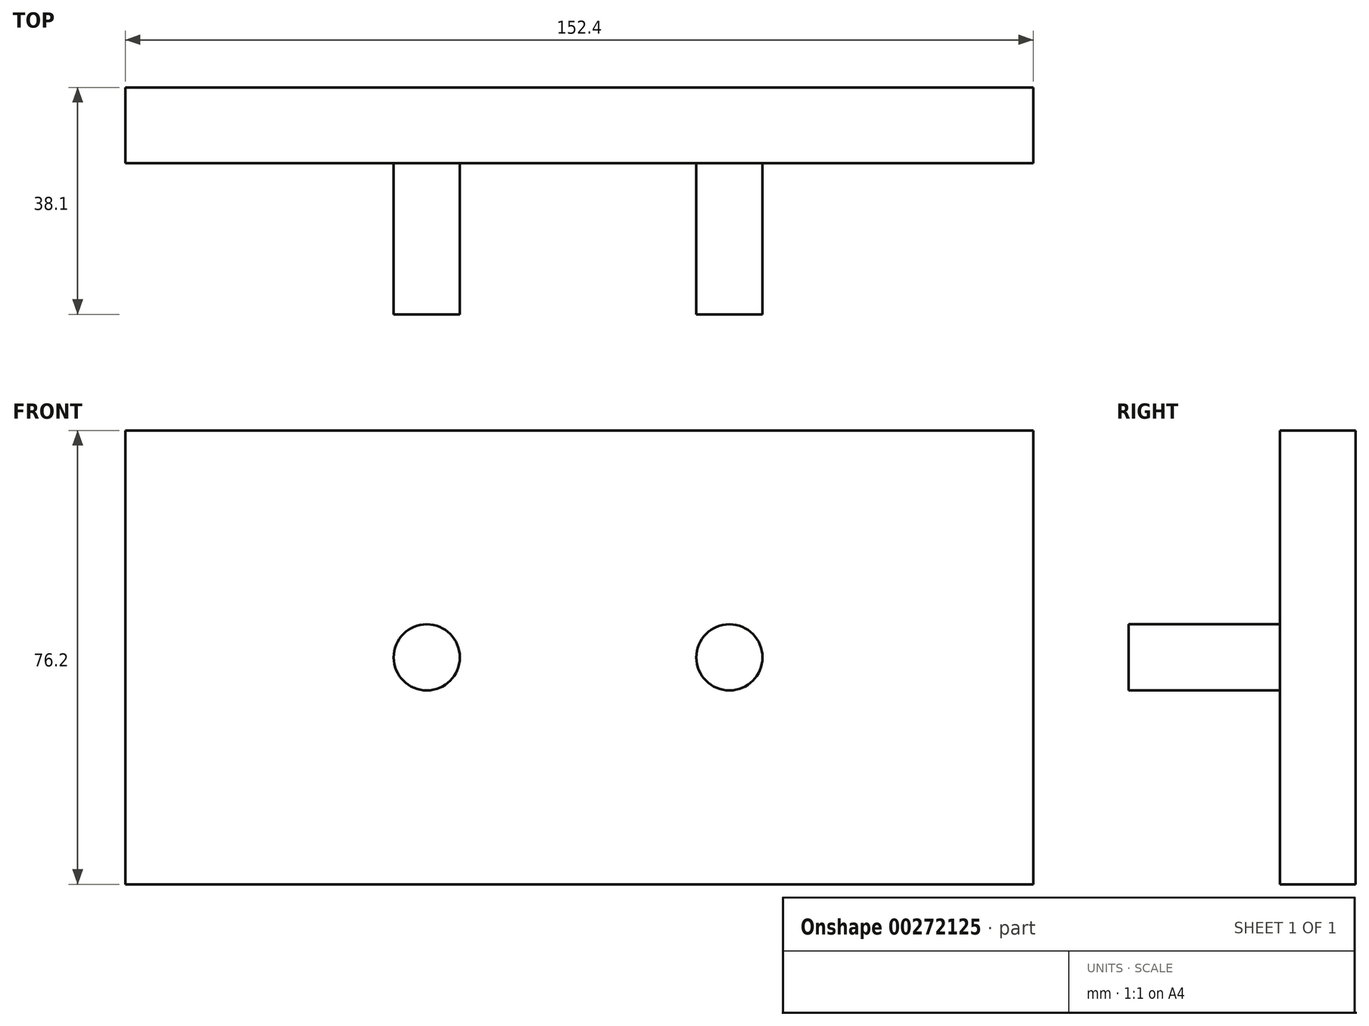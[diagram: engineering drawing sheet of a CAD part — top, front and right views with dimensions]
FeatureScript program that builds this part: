
annotation { "Feature Type Name" : "Feature", "Feature Type Description" : "" }
export const myFeature = defineFeature(function(context is Context, id is Id, definition is map)
    precondition{}
    {
        {
            var Q0;
            Q0=qCreatedBy(makeId("Front.planeOp"),FACE);
            var sketch = newSketch(context, id + "F0", { "sketchPlane" : qUnion([Q0])});
            skLineSegment(sketch, "E0.bottom", {"start": v(76.2, 38.1) * mm, "end": v(-76.2, 38.1) * mm});
            skLineSegment(sketch, "E0.top", {"start": v(76.2, -38.1) * mm, "end": v(-76.2, -38.1) * mm});
            skLineSegment(sketch, "E0.left", {"start": v(76.2, 38.1) * mm, "end": v(76.2, -38.1) * mm});
            skLineSegment(sketch, "E0.right", {"start": v(-76.2, 38.1) * mm, "end": v(-76.2, -38.1) * mm});
            skPoint(sketch, "E0.middle", {"position": v(0, 0) * mm});
            skSolve(sketch);
        }
        {
            var Q0;
            Q0 = qSketchRegion(id + "F0", true);
            extrude(context, id + "F1", {"entities" : qUnion([Q0]), "depth" : 12.7 * mm});
        }
        {
            var Q0;
            Q0=makeQuery(id+"F1.opExtrude","CAP_FACE",FACE,{"disambiguationData":[OSD([sQuery(id+"F0.wireOp",EDGE,"E0.bottom"),sQuery(id+"F0.wireOp",EDGE,"E0.top"),sQuery(id+"F0.wireOp",EDGE,"E0.left"),sQuery(id+"F0.wireOp",EDGE,"E0.right")])],"isStart":false});
            var sketch = newSketch(context, id + "F2", { "sketchPlane" : qUnion([Q0])});
            skCircle(sketch, "E1", {"center": v(-25.6, 0) * mm, "radius": 5.56 * mm});
            skCircle(sketch, "E2", {"center": v(25.2, 0) * mm, "radius": 5.56 * mm});
            skSolve(sketch);
        }
        {
            var Q0;
            Q0=makeQuery(id+"F2.imprint","IMPRINT",FACE,{"disambiguationData":[TD([[makeQuery(id+"F2.imprint","IMPRINT",EDGE,{"derivedFrom":sQuery(id+"F2.wireOp",EDGE,"E1")}),1.0]])]});
            var Q1;
            Q1=makeQuery(id+"F2.imprint","IMPRINT",FACE,{"disambiguationData":[TD([[makeQuery(id+"F2.imprint","IMPRINT",EDGE,{"derivedFrom":sQuery(id+"F2.wireOp",EDGE,"E2")}),1.0]])]});
            extrude(context, id + "F3", {"entities" : qUnion([Q0, Q1]), "operationType" : NewBodyOperationType.ADD, "depth" : 25.4 * mm});
        }
    });
